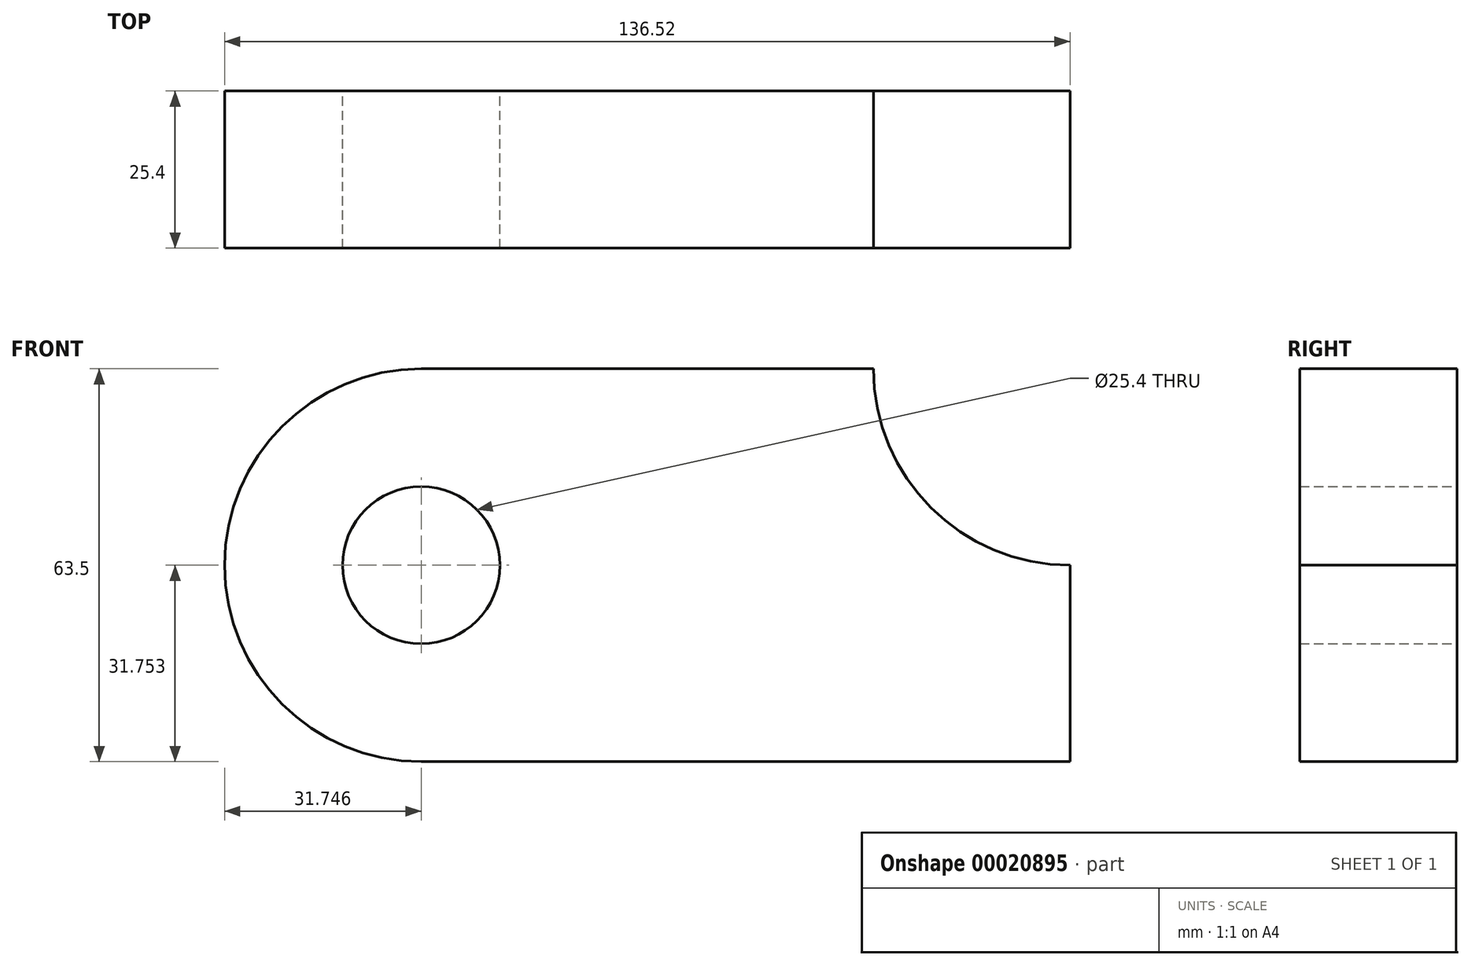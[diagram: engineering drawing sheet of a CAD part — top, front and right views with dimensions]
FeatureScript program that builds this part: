
annotation { "Feature Type Name" : "Feature", "Feature Type Description" : "" }
export const myFeature = defineFeature(function(context is Context, id is Id, definition is map)
    precondition{}
    {
        {
            var Q0;
            Q0=qCreatedBy(makeId("Front.planeOp"),FACE);
            var sketch = newSketch(context, id + "F0", { "sketchPlane" : qUnion([Q0])});
            skLineSegment(sketch, "E0.bottom", {"start": v(-38.82, 36.4) * mm, "end": v(34.2, 36.4) * mm});
            skLineSegment(sketch, "E0.top", {"start": v(-38.82, -27.1) * mm, "end": v(65.95, -27.1) * mm});
            skLineSegment(sketch, "E0.left", {"start": v(-38.82, 36.4) * mm, "end": v(-38.82, -27.1) * mm});
            skLineSegment(sketch, "E0.right", {"start": v(65.95, 4.65) * mm, "end": v(65.95, -27.1) * mm});
            skArc(sketch, "E1", {"start": v(-38.82, 36.4) * mm, "mid": v(-70.57, 4.65) * mm, "end": v(-38.82, -27.1) * mm});
            skCircle(sketch, "E2", {"center": v(-38.82, 4.65) * mm, "radius": 12.7 * mm});
            skArc(sketch, "E3", {"start": v(34.2, 36.4) * mm, "mid": v(43.5, 13.95) * mm, "end": v(65.95, 4.65) * mm});
            skSolve(sketch);
        }
        {
            var Q0;
            {var subQ6=sQuery(id+"F0.wireOp",EDGE,"E0.bottom");Q0=makeQuery(id+"F0.imprint","IMPRINT",FACE,{"disambiguationData":[TD([[makeQuery(id+"F0.imprint","IMPRINT",EDGE,{"derivedFrom":subQ6}),-1.0]])]});}
            var Q1;
            {var subQ4=sQuery(id+"F0.wireOp",EDGE,"E1");Q1=makeQuery(id+"F0.imprint","IMPRINT",FACE,{"disambiguationData":[TD([[makeQuery(id+"F0.imprint","IMPRINT",EDGE,{"derivedFrom":subQ4}),1.0]])]});}
            extrude(context, id + "F1", {"entities" : qUnion([Q0, Q1]), "depth" : 25.4 * mm});
        }
    });
